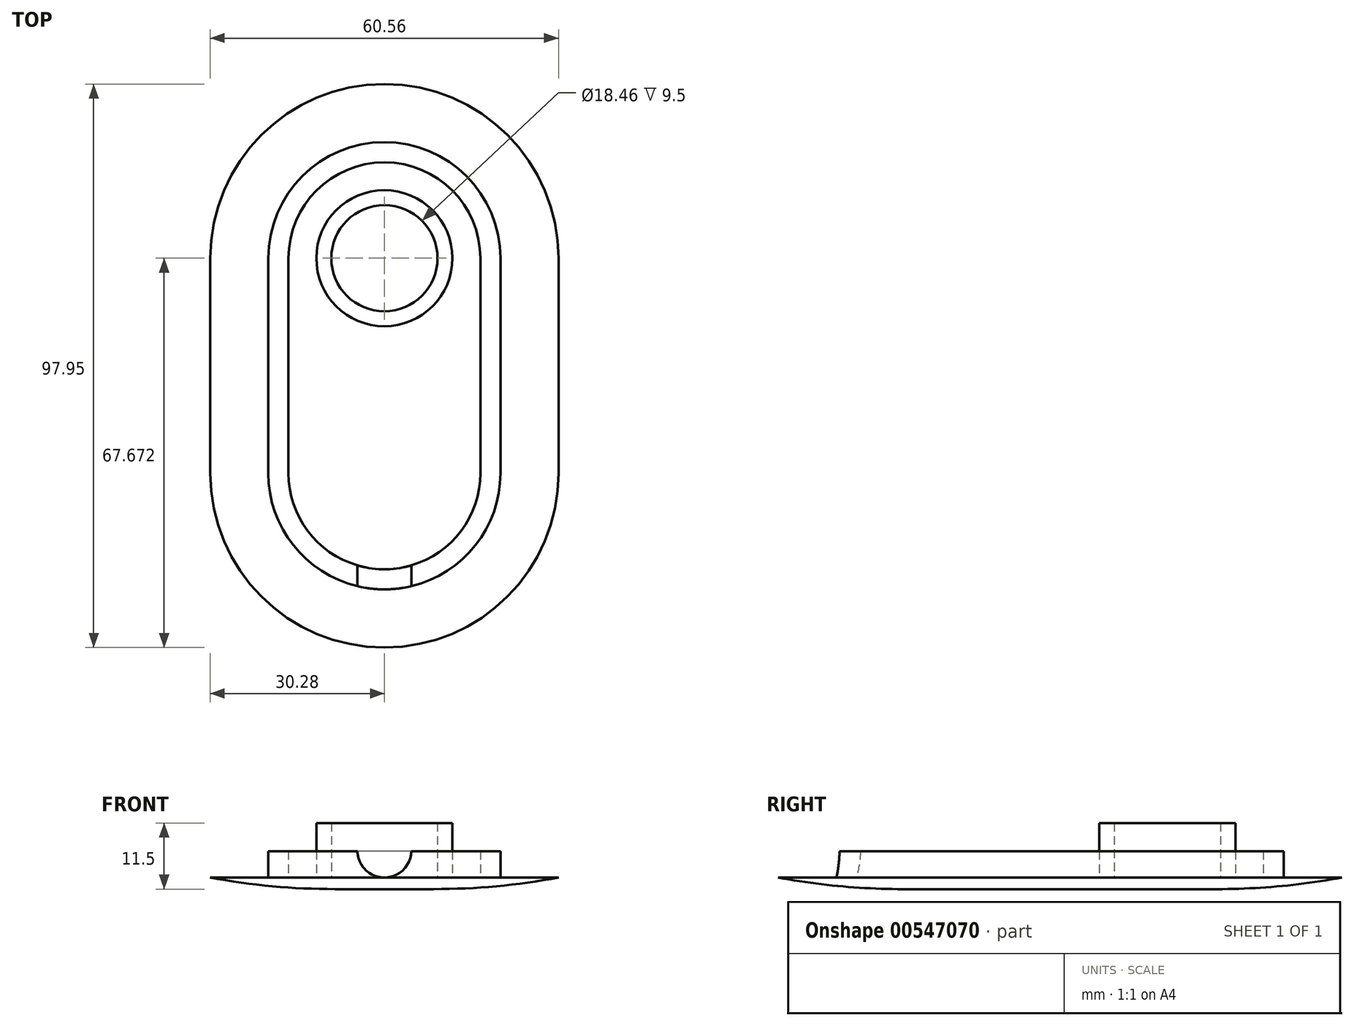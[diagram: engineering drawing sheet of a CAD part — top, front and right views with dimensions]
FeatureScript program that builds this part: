
annotation { "Feature Type Name" : "Feature", "Feature Type Description" : "" }
export const myFeature = defineFeature(function(context is Context, id is Id, definition is map)
    precondition{}
    {
        {
            var Q0;
            Q0=qCreatedBy(makeId("Top.planeOp"),FACE);
            var sketch = newSketch(context, id + "F0", { "sketchPlane" : qUnion([Q0])});
            skArc(sketch, "E0", {"start": v(20.18, 37.4) * mm, "mid": v(0, 57.57) * mm, "end": v(-20.18, 37.4) * mm});
            skLineSegment(sketch, "E1", {"start": v(-20.18, 37.4) * mm, "end": v(-20.18, 0) * mm});
            skLineSegment(sketch, "E2", {"start": v(20.18, 37.4) * mm, "end": v(20.18, 0) * mm});
            skArc(sketch, "E3", {"start": v(-20.18, 0) * mm, "mid": v(0, -20.18) * mm, "end": v(20.18, 0) * mm});
            skArc(sketch, "E4.0", {"start": v(30.28, 37.4) * mm, "mid": v(0, 67.67) * mm, "end": v(-30.28, 37.4) * mm});
            skLineSegment(sketch, "E4.1", {"start": v(30.28, 37.4) * mm, "end": v(30.28, 0) * mm});
            skArc(sketch, "E4.2", {"start": v(-30.28, 0) * mm, "mid": v(0, -30.28) * mm, "end": v(30.28, 0) * mm});
            skLineSegment(sketch, "E4.3", {"start": v(-30.28, 37.4) * mm, "end": v(-30.28, 0) * mm});
            skLineSegment(sketch, "E5.0", {"start": v(-16.68, 37.4) * mm, "end": v(-16.68, 0) * mm});
            skArc(sketch, "E5.1", {"start": v(16.68, 37.4) * mm, "mid": v(0, 54.07) * mm, "end": v(-16.68, 37.4) * mm});
            skLineSegment(sketch, "E5.2", {"start": v(16.68, 37.4) * mm, "end": v(16.68, 0) * mm});
            skArc(sketch, "E5.3", {"start": v(-16.68, 0) * mm, "mid": v(0, -16.68) * mm, "end": v(16.68, 0) * mm});
            skSolve(sketch);
        }
        {
            var Q0;
            Q0=makeQuery(id+"F0.imprint","IMPRINT",FACE,{"disambiguationData":[TD([[makeQuery(id+"F0.imprint","IMPRINT",EDGE,{"derivedFrom":sQuery(id+"F0.wireOp",EDGE,"E0")}),-1.0]])]});
            var Q1;
            Q1=makeQuery(id+"F0.imprint","IMPRINT",FACE,{"disambiguationData":[TD([[makeQuery(id+"F0.imprint","IMPRINT",EDGE,{"derivedFrom":sQuery(id+"F0.wireOp",EDGE,"E5.0")}),1.0]])]});
            var Q2;
            Q2=makeQuery(id+"F0.imprint","IMPRINT",FACE,{"disambiguationData":[TD([[makeQuery(id+"F0.imprint","IMPRINT",EDGE,{"derivedFrom":sQuery(id+"F0.wireOp",EDGE,"E0")}),1.0]])]});
            extrude(context, id + "F1", {"entities" : qUnion([Q0, Q1, Q2]), "oppositeDirection" : true, "depth" : 2 * mm, "offsetDistance" : 25 * mm});
        }
        {
            var Q0;
            Q0=makeQuery(id+"F0.imprint","IMPRINT",FACE,{"disambiguationData":[TD([[makeQuery(id+"F0.imprint","IMPRINT",EDGE,{"derivedFrom":sQuery(id+"F0.wireOp",EDGE,"E0")}),1.0]])]});
            extrude(context, id + "F2", {"entities" : qUnion([Q0]), "operationType" : NewBodyOperationType.ADD, "depth" : 4.6 * mm, "offsetDistance" : 25 * mm});
        }
        {
            var Q0;
            Q0=makeQuery(id+"F1.opExtrude","CAP_EDGE",EDGE,{"disambiguationData":[OSD([sQuery(id+"F0.wireOp",EDGE,"E4.1")])],"isStart":false});
            fillet(context, id + "F3", {"entities" : qUnion([Q0]), "radius" : 118.54 * mm, "tangentPropagation" : true, "allowEdgeOverflow" : false});
        }
        {
            var Q0;
            Q0=qCreatedBy(makeId("Front.planeOp"),FACE);
            var sketch = newSketch(context, id + "F4", { "sketchPlane" : qUnion([Q0])});
            skCircle(sketch, "E6", {"center": v(0, 4.7) * mm, "radius": 4.69 * mm});
            skSolve(sketch);
        }
        {
            var Q0;
            Q0 = qSketchRegion(id + "F4", true);
            extrude(context, id + "F5", {"entities" : qUnion([Q0]), "operationType" : NewBodyOperationType.REMOVE, "depth" : 25 * mm, "offsetDistance" : 25 * mm});
        }
        {
            var Q0;
            Q0=makeQuery(id+"F2.boolean.opBoolean","SPLIT",FACE,{"disambiguationData":[TD([makeQuery(id+"F2.opExtrude","SWEPT_FACE",FACE,{"disambiguationData":[OSD([sQuery(id+"F0.wireOp",EDGE,"E5.0")])]})])],"derivedFrom":makeQuery(id+"F1.opExtrude","CAP_FACE",FACE,{"disambiguationData":[OSD([sQuery(id+"F0.wireOp",EDGE,"E4.0"),sQuery(id+"F0.wireOp",EDGE,"E4.1"),sQuery(id+"F0.wireOp",EDGE,"E4.2"),sQuery(id+"F0.wireOp",EDGE,"E4.3")])],"isStart":true})});
            var sketch = newSketch(context, id + "F6", { "sketchPlane" : qUnion([Q0])});
            skCircle(sketch, "E7", {"center": v(0, 37.4) * mm, "radius": 11.83 * mm});
            skCircle(sketch, "E8.0", {"center": v(0, 37.4) * mm, "radius": 9.23 * mm});
            skSolve(sketch);
        }
        {
            var Q0;
            Q0=makeQuery(id+"F6.imprint","IMPRINT",FACE,{"disambiguationData":[TD([[makeQuery(id+"F6.imprint","IMPRINT",EDGE,{"derivedFrom":sQuery(id+"F6.wireOp",EDGE,"E7")}),1.0]])]});
            extrude(context, id + "F7", {"entities" : qUnion([Q0]), "operationType" : NewBodyOperationType.ADD, "depth" : 9.5 * mm, "offsetDistance" : 25 * mm});
        }
    });
